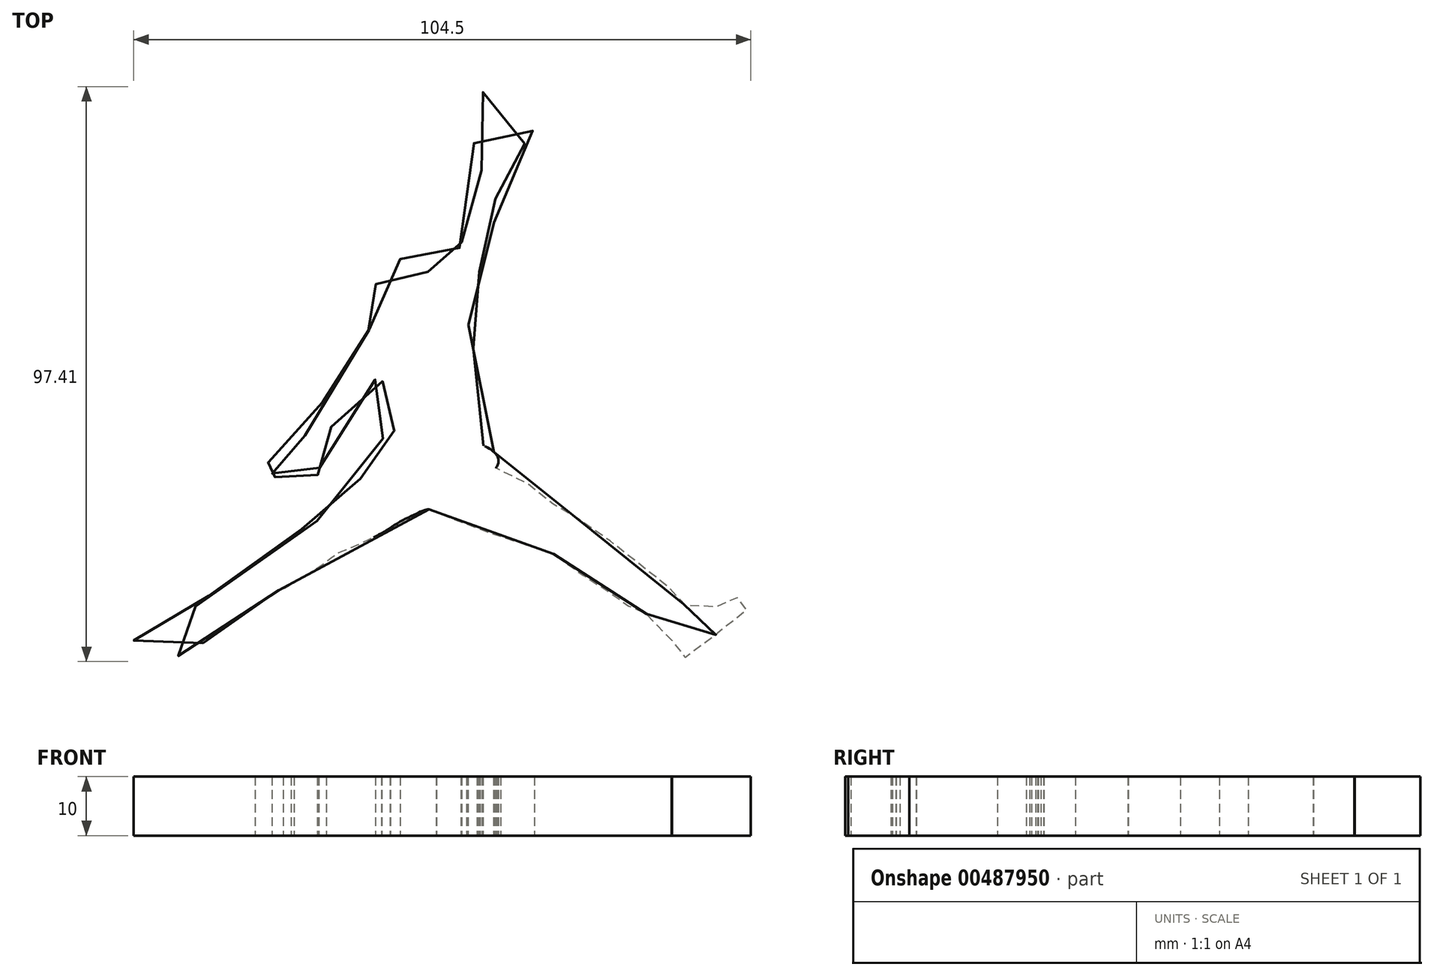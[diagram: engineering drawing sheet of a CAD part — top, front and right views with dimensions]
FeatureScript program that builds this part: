
annotation { "Feature Type Name" : "Feature", "Feature Type Description" : "" }
export const myFeature = defineFeature(function(context is Context, id is Id, definition is map)
    precondition{}
    {
        {
            var Q0;
            Q0=qCreatedBy(makeId("Top.planeOp"),FACE);
            var sketch = newSketch(context, id + "F0", { "sketchPlane" : qUnion([Q0])});
            skFitSpline(sketch, "E0", {"points": [v(0, -19.8) * mm, v(0.2, -19.83) * mm, v(0.48, -19.99) * mm, v(1.1, -20.32) * mm, v(2.32, -20.88) * mm, v(3.56, -21.27) * mm, v(5.27, -21.74) * mm, v(7.68, -22.78) * mm, v(9.68, -23.51) * mm, v(11.32, -24.32) * mm, v(13.95, -25.3) * mm, v(15.3, -25.56) * mm, v(18.19, -26.14) * mm, v(19.48, -26.44) * mm, v(19.57, -26.65) * mm, v(20.06, -26.91) * mm, v(21.05, -27.34) * mm, v(22.12, -27.94) * mm, v(23.74, -29.2) * mm, v(25.71, -30.67) * mm, v(27.3, -31.83) * mm, v(28.82, -33.03) * mm, v(29.33, -33.3) * mm, v(29.66, -33.44) * mm, v(30.19, -33.56) * mm, v(30.42, -33.56) * mm, v(31.1, -34.2) * mm, v(32.19, -34.96) * mm, v(33.13, -35.66) * mm, v(34.06, -36.37) * mm, v(34.75, -36.83) * mm, v(35.13, -36.98) * mm, v(35.58, -36.98) * mm, v(35.91, -36.98) * mm, v(36.16, -36.98) * mm, v(36.7, -37.44) * mm, v(37.25, -37.84) * mm, v(37.4, -38.04) * mm, v(37.53, -38.3) * mm, v(37.79, -38.55) * mm, v(38.11, -38.88) * mm, v(38.42, -39.16) * mm, v(38.8, -39.59) * mm, v(39.15, -39.72) * mm, v(39.3, -40) * mm, v(39.44, -40.32) * mm, v(40.42, -41.42) * mm, v(40.69, -41.76) * mm, v(41.12, -42) * mm, v(41.13, -42.31) * mm, v(41.37, -42.96) * mm, v(41.75, -43.62) * mm, v(42.58, -45) * mm, v(43.18, -45) * mm, v(44.19, -44.26) * mm, v(45.57, -43.07) * mm, v(47.18, -41.78) * mm, v(49.3, -40.67) * mm, v(51.32, -39.06) * mm, v(52.93, -37.54) * mm, v(54.5, -35.98) * mm, v(54.31, -35.5) * mm, v(53.92, -35.14) * mm, v(53.48, -34.9) * mm, v(52.87, -34.71) * mm, v(52.07, -34.83) * mm, v(51.46, -35.2) * mm, v(50.72, -35.63) * mm, v(50.03, -36.06) * mm, v(49.52, -36.26) * mm, v(48.35, -36.32) * mm, v(46.9, -36.34) * mm, v(45.76, -36.31) * mm, v(44.32, -36.3) * mm, v(43.12, -35.83) * mm, v(42.05, -34.72) * mm, v(41.47, -34.5) * mm, v(41.02, -34.03) * mm, v(40.88, -33.43) * mm, v(40.56, -33) * mm, v(39.17, -32.11) * mm, v(37.3, -30.2) * mm, v(36.82, -29.96) * mm, v(35.4, -28.76) * mm, v(33.62, -27.29) * mm, v(31.48, -25.76) * mm, v(29, -23.88) * mm, v(27.27, -22.71) * mm, v(25.08, -21.3) * mm, v(23.68, -20.35) * mm, v(23.38, -20.22) * mm, v(22.62, -20.12) * mm, v(21.98, -19.97) * mm, v(20.96, -18.83) * mm, v(19.69, -17.68) * mm, v(18.54, -16.8) * mm, v(17.36, -15.88) * mm, v(15.82, -14.96) * mm, v(14.2, -14.23) * mm, v(13, -13.6) * mm, v(11.37, -12.78) * mm, v(11.5, -12.6) * mm, v(11.63, -12.33) * mm, v(11.73, -12.03) * mm, v(11.78, -11.66) * mm, v(11.78, -11.43) * mm, v(11.72, -11.1) * mm, v(11.47, -10.57) * mm, v(11.04, -10.14) * mm, v(10.46, -9.65) * mm, v(9.6, -9.16) * mm, v(9.23, -9.02) * mm, v(8.92, -8.2) * mm, v(8.4, -7.03) * mm, v(8.55, -6.5) * mm, v(8.93, -4.45) * mm, v(9.15, -2.65) * mm, v(9.15, -0.27) * mm, v(9.04, 3.33) * mm, v(8.75, 5.3) * mm, v(7.8, 6.92) * mm, v(7.17, 8.5) * mm, v(6.73, 10.55) * mm, v(6.7, 11.32) * mm, v(6.63, 12.71) * mm, v(6.92, 13.58) * mm, v(7.53, 15) * mm, v(7.96, 16.47) * mm, v(8.12, 17.37) * mm, v(8.18, 18.32) * mm, v(8.17, 19) * mm, v(8.19, 19.73) * mm, v(8.4, 20.15) * mm, v(8.63, 20.9) * mm, v(8.65, 21.68) * mm, v(8.69, 22.57) * mm, v(9.04, 23.14) * mm, v(9.28, 23.9) * mm, v(9.63, 25.04) * mm, v(10.14, 27.67) * mm, v(10.56, 28.03) * mm, v(10.97, 28.41) * mm, v(10.97, 29.06) * mm, v(11.35, 30.86) * mm, v(11.47, 32.16) * mm, v(11.26, 32.93) * mm, v(11.38, 34.34) * mm, v(11.55, 35.53) * mm, v(11.75, 36.87) * mm, v(11.8, 37.9) * mm, v(12.08, 38.72) * mm, v(12.08, 39.7) * mm, v(11.8, 40.14) * mm, v(11.77, 40.47) * mm, v(11.97, 40.67) * mm, v(12.41, 40.67) * mm, v(13.83, 40.86) * mm, v(15.35, 41.58) * mm, v(16.46, 42.42) * mm, v(17.28, 43.69) * mm, v(17.85, 45.37) * mm, v(17.85, 46.66) * mm, v(17.7, 47.76) * mm, v(16.45, 50) * mm, v(14.85, 51.2) * mm, v(13.17, 51.76) * mm, v(11.4, 51.72) * mm, v(9.32, 51) * mm, v(7.84, 49.76) * mm, v(7.04, 48.07) * mm, v(6.52, 46.47) * mm, v(6.8, 44.8) * mm, v(7.12, 43.59) * mm, v(7.52, 42.5) * mm, v(7.92, 41.63) * mm, v(8.48, 40.63) * mm, v(8.8, 39.59) * mm, v(9, 38.7) * mm, v(8.8, 37.22) * mm, v(8.32, 35.02) * mm, v(8, 33.7) * mm, v(7.64, 33.68) * mm, v(7.49, 33.28) * mm, v(6.98, 31.54) * mm, v(6.42, 29.74) * mm, v(6.4, 29.36) * mm, v(6.52, 29.25) * mm, v(6.28, 28.69) * mm, v(5.8, 27.72) * mm, v(5.47, 26.9) * mm, v(5.43, 25.97) * mm, v(5.5, 25.32) * mm, v(4.93, 23.98) * mm, v(4.28, 21.56) * mm, v(3.93, 20.36) * mm, v(2.62, 19.25) * mm, v(1.97, 17.75) * mm, v(1.83, 18.14) * mm, v(1.6, 18.68) * mm, v(1.35, 18.93) * mm, v(1.25, 19.12) * mm, v(1.26, 19.84) * mm, v(1.16, 20) * mm, v(0.85, 20.1) * mm, v(0, 20.35) * mm, v(-0.12, 20.4) * mm, v(-0.3, 20.79) * mm, v(-0.65, 20.9) * mm, v(-0.93, 21) * mm, v(-1.4, 21.55) * mm, v(-2.02, 22.07) * mm, v(-2.8, 22.45) * mm, v(-3.7, 22.65) * mm, v(-4.58, 22.65) * mm, v(-5.6, 22.44) * mm, v(-5.99, 22.27) * mm, v(-6.86, 21.68) * mm, v(-7.56, 20.92) * mm, v(-8.27, 19.95) * mm, v(-9, 18.2) * mm, v(-8.94, 16.83) * mm, v(-8.44, 15.6) * mm, v(-7.7, 14.82) * mm, v(-7, 14.19) * mm, v(-6.7, 13.85) * mm, v(-6.6, 13.68) * mm, v(-6.76, 13.45) * mm, v(-6.84, 12.99) * mm, v(-6.96, 12.6) * mm, v(-7.42, 12.08) * mm, v(-8.13, 11.5) * mm, v(-8.53, 11.19) * mm, v(-8.97, 11.19) * mm, v(-9.5, 10.92) * mm, v(-10.2, 10.58) * mm, v(-10.93, 9.51) * mm, v(-11.95, 7.84) * mm, v(-12.98, 6.05) * mm, v(-13.52, 4.9) * mm, v(-13.7, 4.78) * mm, v(-14.25, 4.13) * mm, v(-14.77, 3.23) * mm, v(-15.14, 2.47) * mm, v(-15.35, 1.54) * mm, v(-15.93, 1.12) * mm, v(-17.56, -1.04) * mm, v(-18.35, -2.14) * mm, v(-19.01, -3.42) * mm, v(-20.12, -5.37) * mm, v(-20.55, -6.26) * mm, v(-20.93, -7.15) * mm, v(-21.08, -7.54) * mm, v(-21.83, -8.35) * mm, v(-22.7, -9.2) * mm, v(-23.65, -10.32) * mm, v(-25.58, -11.33) * mm, v(-26.46, -11.67) * mm, v(-28.16, -11.97) * mm, v(-29.17, -11.95) * mm, v(-29.43, -12.14) * mm, v(-29.32, -12.52) * mm, v(-29, -12.68) * mm, v(-27.78, -12.87) * mm, v(-26.67, -12.85) * mm, v(-25.56, -12.66) * mm, v(-24.78, -12.47) * mm, v(-24.7, -12.59) * mm, v(-24.87, -12.85) * mm, v(-25.4, -13.1) * mm, v(-25.98, -13.34) * mm, v(-26.48, -13.58) * mm, v(-26.53, -14) * mm, v(-26.24, -14.29) * mm, v(-25.72, -14.29) * mm, v(-24.7, -13.98) * mm, v(-23.6, -13.65) * mm, v(-22.87, -13.37) * mm, v(-22.96, -13.82) * mm, v(-23.2, -14.24) * mm, v(-23.36, -14.69) * mm, v(-23.05, -14.93) * mm, v(-22.32, -14.76) * mm, v(-21.54, -13.82) * mm, v(-20.95, -13.23) * mm, v(-20.53, -12.99) * mm, v(-20.12, -13.18) * mm, v(-19.86, -13.58) * mm, v(-19.18, -13.89) * mm, v(-18.45, -14) * mm, v(-17.79, -14) * mm, v(-17.43, -13.72) * mm, v(-17.38, -13.3) * mm, v(-17.64, -13.01) * mm, v(-18.33, -12.87) * mm, v(-18.7, -12.54) * mm, v(-18.92, -12) * mm, v(-18.68, -11.57) * mm, v(-18.87, -10.93) * mm, v(-18.85, -9.99) * mm, v(-18.42, -8.8) * mm, v(-17.71, -7.37) * mm, v(-17.02, -6.38) * mm, v(-16.6, -5.89) * mm, v(-15.45, -5.26) * mm, v(-13.94, -3.96) * mm, v(-12.68, -2.73) * mm, v(-11.66, -1.05) * mm, v(-10.86, 0.42) * mm, v(-10.74, 0.83) * mm, v(-10.32, 0.94) * mm, v(-9.56, 1.34) * mm, v(-9.27, 1.78) * mm, v(-8.99, 2.36) * mm, v(-8.7, 2.32) * mm, v(-8.16, 2.3) * mm, v(-7.93, 2.01) * mm, v(-7.62, 1.44) * mm, v(-7.2, 0.76) * mm, v(-6.8, 0.19) * mm, v(-6.56, -0.15) * mm, v(-6.51, -0.63) * mm, v(-6.5, -1.2) * mm, v(-6.23, -1.5) * mm, v(-5.87, -2) * mm, v(-5.69, -2.18) * mm, v(-5.6, -2.7) * mm, v(-5.39, -3.44) * mm, v(-5.2, -4.1) * mm, v(-4.96, -4.71) * mm, v(-4.88, -5.07) * mm, v(-5.35, -5.55) * mm, v(-5.75, -6.2) * mm, v(-5.9, -6.54) * mm, v(-6.45, -6.58) * mm, v(-6.95, -6.78) * mm, v(-7.52, -7.26) * mm, v(-7.82, -7.89) * mm, v(-8.02, -8.63) * mm, v(-8.02, -9.27) * mm, v(-8.07, -11.5) * mm, v(-8.53, -12.18) * mm, v(-9.13, -12.78) * mm, v(-9.73, -13.06) * mm, v(-10.45, -13.22) * mm, v(-10.95, -13.6) * mm, v(-11.33, -14.19) * mm, v(-11.53, -14.49) * mm, v(-12.87, -15.47) * mm, v(-14.13, -16.47) * mm, v(-15.42, -17.68) * mm, v(-16.6, -19.1) * mm, v(-17.56, -20.03) * mm, v(-18.21, -21.16) * mm, v(-18.58, -21.64) * mm, v(-18.96, -21.75) * mm, v(-19.47, -21.82) * mm, v(-20.07, -22.02) * mm, v(-20.92, -22.52) * mm, v(-21.49, -23.06) * mm, v(-21.94, -23.46) * mm, v(-24.7, -24.7) * mm, v(-28.08, -26.7) * mm, v(-30.64, -28.42) * mm, v(-32.43, -29.87) * mm, v(-33.58, -30.95) * mm, v(-35.47, -32.92) * mm, v(-36.76, -34.15) * mm, v(-38.14, -35.01) * mm, v(-39.62, -36.3) * mm, v(-40.97, -37.56) * mm, v(-42.2, -38.67) * mm, v(-43.45, -39.22) * mm, v(-44.68, -39.65) * mm, v(-45.7, -39.83) * mm, v(-46.8, -40.02) * mm, v(-48.3, -40.26) * mm, v(-49.8, -41.48) * mm, v(-49.93, -42.56) * mm, v(-49.26, -43.64) * mm, v(-47.97, -44.8) * mm, v(-46.76, -45.47) * mm, v(-44.93, -45.47) * mm, v(-43.58, -44.86) * mm, v(-42.36, -44.66) * mm, v(-41.07, -44.66) * mm, v(-39.86, -44.39) * mm, v(-38.98, -43.3) * mm, v(-38.37, -42.56) * mm, v(-37.76, -42.3) * mm, v(-37.02, -41.75) * mm, v(-36.27, -40.26) * mm, v(-35.33, -39.86) * mm, v(-34.51, -38.98) * mm, v(-33.77, -38.57) * mm, v(-32.55, -37.9) * mm, v(-32.14, -37.58) * mm, v(-31.84, -37.74) * mm, v(-31.3, -37.86) * mm, v(-30.89, -37.67) * mm, v(-30.39, -37.22) * mm, v(-25.67, -33.66) * mm, v(-25, -33.4) * mm, v(-22.17, -31.83) * mm, v(-19.98, -30.47) * mm, v(-17.05, -28.43) * mm, v(-15.38, -27.23) * mm, v(-13.6, -26.45) * mm, v(-9.74, -24.72) * mm, v(-7.28, -23.42) * mm, v(-4.62, -21.74) * mm, v(-2.1, -20.54) * mm, v(-0.7, -19.91) * mm, v(0, -19.8) * mm]});
            skSolve(sketch);
        }
        {
            var Q0;
            Q0=makeQuery(id+"F0.imprint","IMPRINT",FACE,{"disambiguationData":[TD([[makeQuery(id+"F0.imprint","IMPRINT",EDGE,{"derivedFrom":sQuery(id+"F0.wireOp",EDGE,"E0")}),1.0]])]});
            extrude(context, id + "F1", {"entities" : qUnion([Q0]), "depth" : 10 * mm});
        }
    });
